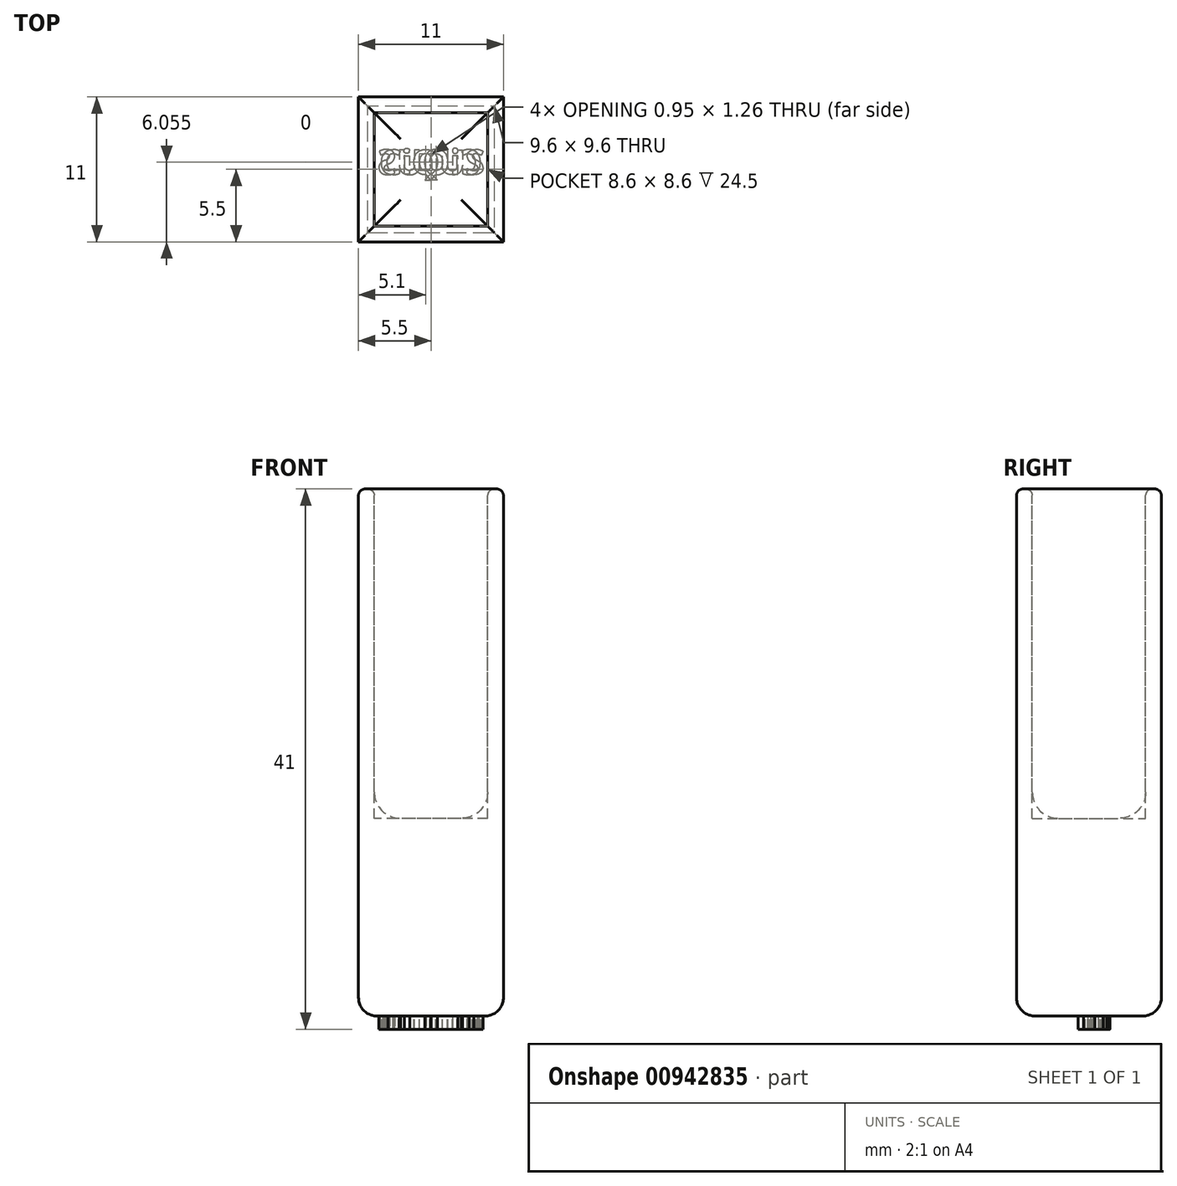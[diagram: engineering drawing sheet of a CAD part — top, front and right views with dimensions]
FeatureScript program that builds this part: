
annotation { "Feature Type Name" : "Feature", "Feature Type Description" : "" }
export const myFeature = defineFeature(function(context is Context, id is Id, definition is map)
    precondition{}
    {
        {
            var Q0;
            Q0=qCreatedBy(makeId("Top.planeOp"),FACE);
            var sketch = newSketch(context, id + "F0", { "sketchPlane" : qUnion([Q0])});
            skLineSegment(sketch, "E0.bottom", {"start": v(-5.5, 5.5) * mm, "end": v(5.5, 5.5) * mm});
            skLineSegment(sketch, "E0.top", {"start": v(-5.5, -5.5) * mm, "end": v(5.5, -5.5) * mm});
            skLineSegment(sketch, "E0.left", {"start": v(-5.5, 5.5) * mm, "end": v(-5.5, -5.5) * mm});
            skLineSegment(sketch, "E0.right", {"start": v(5.5, 5.5) * mm, "end": v(5.5, -5.5) * mm});
            skPoint(sketch, "E0.middle", {"position": v(0, 0) * mm});
            skSolve(sketch);
        }
        {
            var Q0;
            Q0=makeQuery(id+"F0.imprint","IMPRINT",FACE,{"disambiguationData":[TD([[makeQuery(id+"F0.imprint","IMPRINT",EDGE,{"derivedFrom":sQuery(id+"F0.wireOp",EDGE,"E0.bottom")}),-1.0]])]});
            extrude(context, id + "F1", {"entities" : qUnion([Q0]), "depth" : 40 * mm, "offsetDistance" : 25.4 * mm});
        }
        {
            var Q0;
            Q0=makeQuery(id+"F1.opExtrude","CAP_FACE",FACE,{"disambiguationData":[OSD([sQuery(id+"F0.wireOp",EDGE,"E0.bottom"),sQuery(id+"F0.wireOp",EDGE,"E0.top"),sQuery(id+"F0.wireOp",EDGE,"E0.left"),sQuery(id+"F0.wireOp",EDGE,"E0.right")])],"isStart":false});
            var sketch = newSketch(context, id + "F2", { "sketchPlane" : qUnion([Q0])});
            skLineSegment(sketch, "E1.bottom", {"start": v(4.3, -4.3) * mm, "end": v(-4.3, -4.3) * mm});
            skLineSegment(sketch, "E1.top", {"start": v(4.3, 4.3) * mm, "end": v(-4.3, 4.3) * mm});
            skLineSegment(sketch, "E1.left", {"start": v(4.3, -4.3) * mm, "end": v(4.3, 4.3) * mm});
            skLineSegment(sketch, "E1.right", {"start": v(-4.3, -4.3) * mm, "end": v(-4.3, 4.3) * mm});
            skPoint(sketch, "E1.middle", {"position": v(0, 0) * mm});
            skSolve(sketch);
        }
        {
            var Q0;
            Q0=makeQuery(id+"F2.imprint","IMPRINT",FACE,{"disambiguationData":[TD([[makeQuery(id+"F2.imprint","IMPRINT",EDGE,{"derivedFrom":sQuery(id+"F2.wireOp",EDGE,"E1.bottom")}),-1.0]])]});
            extrude(context, id + "F3", {"entities" : qUnion([Q0]), "operationType" : NewBodyOperationType.REMOVE, "oppositeDirection" : true, "depth" : 25 * mm, "offsetDistance" : 25 * mm});
        }
        {
            var Q0;
            Q0=makeQuery(id+"F1.opExtrude","CAP_FACE",FACE,{"disambiguationData":[OSD([sQuery(id+"F0.wireOp",EDGE,"E0.bottom"),sQuery(id+"F0.wireOp",EDGE,"E0.top"),sQuery(id+"F0.wireOp",EDGE,"E0.left"),sQuery(id+"F0.wireOp",EDGE,"E0.right")])],"isStart":false});
            fillet(context, id + "F4", {"entities" : qUnion([Q0]), "radius" : .5 * mm, "tangentPropagation" : true, "allowEdgeOverflow" : false});
        }
        {
            var Q0;
            Q0=makeQuery(id+"F1.opExtrude","CAP_FACE",FACE,{"disambiguationData":[OSD([sQuery(id+"F0.wireOp",EDGE,"E0.bottom"),sQuery(id+"F0.wireOp",EDGE,"E0.top"),sQuery(id+"F0.wireOp",EDGE,"E0.left"),sQuery(id+"F0.wireOp",EDGE,"E0.right")])],"isStart":true});
            fillet(context, id + "F5", {"entities" : qUnion([Q0]), "radius" : 1.4 * mm, "tangentPropagation" : true, "allowEdgeOverflow" : false});
        }
        {
            var Q0;
            Q0=makeQuery(id+"F3.boolean.opBoolean","COPY",FACE,{"derivedFrom":makeQuery(id+"F3.opExtrude","CAP_FACE",FACE,{"disambiguationData":[OSD([sQuery(id+"F2.wireOp",EDGE,"E1.bottom"),sQuery(id+"F2.wireOp",EDGE,"E1.top"),sQuery(id+"F2.wireOp",EDGE,"E1.left"),sQuery(id+"F2.wireOp",EDGE,"E1.right")])],"isStart":false})});
            fillet(context, id + "F6", {"entities" : qUnion([Q0]), "radius" : 2 * mm, "tangentPropagation" : true, "allowEdgeOverflow" : false});
        }
        {
            var Q0;
            Q0=qCreatedBy(makeId("Top.planeOp"),FACE);
            var sketch = newSketch(context, id + "F7", { "sketchPlane" : qUnion([Q0])});
            skText(sketch, "E2", { "text": "CiQUS", "fontName": "OpenSans-Bold.ttf"});
            const initialGuessF7  = {"E2": [-0.0039, -0.00038, 1, 0, 0.00188]};
            skSetInitialGuess(sketch, initialGuessF7);
            skSolve(sketch);
        }
        {
            var Q0;
            Q0 = qSketchRegion(id + "F7", true);
            extrude(context, id + "F8", {"entities" : qUnion([Q0]), "depth" : -1 * mm, "offsetDistance" : 25 * mm});
        }
        {
            var Q0;
            Q0=makeQuery(id+"F8.opExtrude","SWEPT_BODY",BODY,{"disambiguationData":[OSD([sQuery(id+"F7.wireOp",EDGE,"E2.sketch_text.stroke-57"),sQuery(id+"F7.wireOp",EDGE,"E2.sketch_text.stroke-58"),sQuery(id+"F7.wireOp",EDGE,"E2.sketch_text.stroke-59"),sQuery(id+"F7.wireOp",EDGE,"E2.sketch_text.stroke-60"),sQuery(id+"F7.wireOp",EDGE,"E2.sketch_text.stroke-61"),sQuery(id+"F7.wireOp",EDGE,"E2.sketch_text.stroke-62"),sQuery(id+"F7.wireOp",EDGE,"E2.sketch_text.stroke-63"),sQuery(id+"F7.wireOp",EDGE,"E2.sketch_text.stroke-64"),sQuery(id+"F7.wireOp",EDGE,"E2.sketch_text.stroke-65"),sQuery(id+"F7.wireOp",EDGE,"E2.sketch_text.stroke-66"),sQuery(id+"F7.wireOp",EDGE,"E2.sketch_text.stroke-67"),sQuery(id+"F7.wireOp",EDGE,"E2.sketch_text.stroke-68"),sQuery(id+"F7.wireOp",EDGE,"E2.sketch_text.stroke-69"),sQuery(id+"F7.wireOp",EDGE,"E2.sketch_text.stroke-70"),sQuery(id+"F7.wireOp",EDGE,"E2.sketch_text.stroke-71"),sQuery(id+"F7.wireOp",EDGE,"E2.sketch_text.stroke-72"),sQuery(id+"F7.wireOp",EDGE,"E2.sketch_text.stroke-73"),sQuery(id+"F7.wireOp",EDGE,"E2.sketch_text.stroke-74"),sQuery(id+"F7.wireOp",EDGE,"E2.sketch_text.stroke-75"),sQuery(id+"F7.wireOp",EDGE,"E2.sketch_text.stroke-76"),sQuery(id+"F7.wireOp",EDGE,"E2.sketch_text.stroke-77"),sQuery(id+"F7.wireOp",EDGE,"E2.sketch_text.stroke-78"),sQuery(id+"F7.wireOp",EDGE,"E2.sketch_text.stroke-79"),sQuery(id+"F7.wireOp",EDGE,"E2.sketch_text.stroke-80"),sQuery(id+"F7.wireOp",EDGE,"E2.sketch_text.stroke-81"),sQuery(id+"F7.wireOp",EDGE,"E2.sketch_text.stroke-82"),sQuery(id+"F7.wireOp",EDGE,"E2.sketch_text.stroke-83"),sQuery(id+"F7.wireOp",EDGE,"E2.sketch_text.stroke-84")])]});
            var Q1;
            Q1=makeQuery(id+"F8.opExtrude","SWEPT_BODY",BODY,{"disambiguationData":[OSD([sQuery(id+"F7.wireOp",EDGE,"E2.sketch_text.stroke-42"),sQuery(id+"F7.wireOp",EDGE,"E2.sketch_text.stroke-43"),sQuery(id+"F7.wireOp",EDGE,"E2.sketch_text.stroke-44"),sQuery(id+"F7.wireOp",EDGE,"E2.sketch_text.stroke-45"),sQuery(id+"F7.wireOp",EDGE,"E2.sketch_text.stroke-46"),sQuery(id+"F7.wireOp",EDGE,"E2.sketch_text.stroke-47"),sQuery(id+"F7.wireOp",EDGE,"E2.sketch_text.stroke-48"),sQuery(id+"F7.wireOp",EDGE,"E2.sketch_text.stroke-49"),sQuery(id+"F7.wireOp",EDGE,"E2.sketch_text.stroke-50"),sQuery(id+"F7.wireOp",EDGE,"E2.sketch_text.stroke-51"),sQuery(id+"F7.wireOp",EDGE,"E2.sketch_text.stroke-52"),sQuery(id+"F7.wireOp",EDGE,"E2.sketch_text.stroke-53"),sQuery(id+"F7.wireOp",EDGE,"E2.sketch_text.stroke-54"),sQuery(id+"F7.wireOp",EDGE,"E2.sketch_text.stroke-55"),sQuery(id+"F7.wireOp",EDGE,"E2.sketch_text.stroke-56")])]});
            var Q2;
            Q2=makeQuery(id+"F8.opExtrude","SWEPT_BODY",BODY,{"disambiguationData":[OSD([sQuery(id+"F7.wireOp",EDGE,"E2.sketch_text.stroke-24"),sQuery(id+"F7.wireOp",EDGE,"E2.sketch_text.stroke-25"),sQuery(id+"F7.wireOp",EDGE,"E2.sketch_text.stroke-26"),sQuery(id+"F7.wireOp",EDGE,"E2.sketch_text.stroke-27"),sQuery(id+"F7.wireOp",EDGE,"E2.sketch_text.stroke-28"),sQuery(id+"F7.wireOp",EDGE,"E2.sketch_text.stroke-29"),sQuery(id+"F7.wireOp",EDGE,"E2.sketch_text.stroke-30"),sQuery(id+"F7.wireOp",EDGE,"E2.sketch_text.stroke-31"),sQuery(id+"F7.wireOp",EDGE,"E2.sketch_text.stroke-32"),sQuery(id+"F7.wireOp",EDGE,"E2.sketch_text.stroke-33"),sQuery(id+"F7.wireOp",EDGE,"E2.sketch_text.stroke-34"),sQuery(id+"F7.wireOp",EDGE,"E2.sketch_text.stroke-35"),sQuery(id+"F7.wireOp",EDGE,"E2.sketch_text.stroke-36"),sQuery(id+"F7.wireOp",EDGE,"E2.sketch_text.stroke-37"),sQuery(id+"F7.wireOp",EDGE,"E2.sketch_text.stroke-38"),sQuery(id+"F7.wireOp",EDGE,"E2.sketch_text.stroke-39"),sQuery(id+"F7.wireOp",EDGE,"E2.sketch_text.stroke-40"),sQuery(id+"F7.wireOp",EDGE,"E2.sketch_text.stroke-41")])]});
            var Q3;
            Q3=makeQuery(id+"F8.opExtrude","SWEPT_BODY",BODY,{"disambiguationData":[OSD([sQuery(id+"F7.wireOp",EDGE,"E2.sketch_text.stroke-20"),sQuery(id+"F7.wireOp",EDGE,"E2.sketch_text.stroke-21"),sQuery(id+"F7.wireOp",EDGE,"E2.sketch_text.stroke-22"),sQuery(id+"F7.wireOp",EDGE,"E2.sketch_text.stroke-23")])]});
            var Q4;
            Q4=makeQuery(id+"F8.opExtrude","SWEPT_BODY",BODY,{"disambiguationData":[OSD([sQuery(id+"F7.wireOp",EDGE,"E2.sketch_text.stroke-15"),sQuery(id+"F7.wireOp",EDGE,"E2.sketch_text.stroke-16"),sQuery(id+"F7.wireOp",EDGE,"E2.sketch_text.stroke-17"),sQuery(id+"F7.wireOp",EDGE,"E2.sketch_text.stroke-18"),sQuery(id+"F7.wireOp",EDGE,"E2.sketch_text.stroke-19")])]});
            var Q5;
            Q5=makeQuery(id+"F8.opExtrude","SWEPT_BODY",BODY,{"disambiguationData":[OSD([sQuery(id+"F7.wireOp",EDGE,"E2.sketch_text.stroke-0"),sQuery(id+"F7.wireOp",EDGE,"E2.sketch_text.stroke-1"),sQuery(id+"F7.wireOp",EDGE,"E2.sketch_text.stroke-2"),sQuery(id+"F7.wireOp",EDGE,"E2.sketch_text.stroke-3"),sQuery(id+"F7.wireOp",EDGE,"E2.sketch_text.stroke-4"),sQuery(id+"F7.wireOp",EDGE,"E2.sketch_text.stroke-5"),sQuery(id+"F7.wireOp",EDGE,"E2.sketch_text.stroke-6"),sQuery(id+"F7.wireOp",EDGE,"E2.sketch_text.stroke-7"),sQuery(id+"F7.wireOp",EDGE,"E2.sketch_text.stroke-8"),sQuery(id+"F7.wireOp",EDGE,"E2.sketch_text.stroke-9"),sQuery(id+"F7.wireOp",EDGE,"E2.sketch_text.stroke-10"),sQuery(id+"F7.wireOp",EDGE,"E2.sketch_text.stroke-11"),sQuery(id+"F7.wireOp",EDGE,"E2.sketch_text.stroke-12"),sQuery(id+"F7.wireOp",EDGE,"E2.sketch_text.stroke-13"),sQuery(id+"F7.wireOp",EDGE,"E2.sketch_text.stroke-14")])]});
            var Q6;
            Q6=qCreatedBy(makeId("Right.planeOp"),FACE);
            mirror(context, id + "F9", {"entities" : qUnion([Q0, Q1, Q2, Q3, Q4, Q5]), "mirrorPlane" : qUnion([Q6])});
        }
    });
